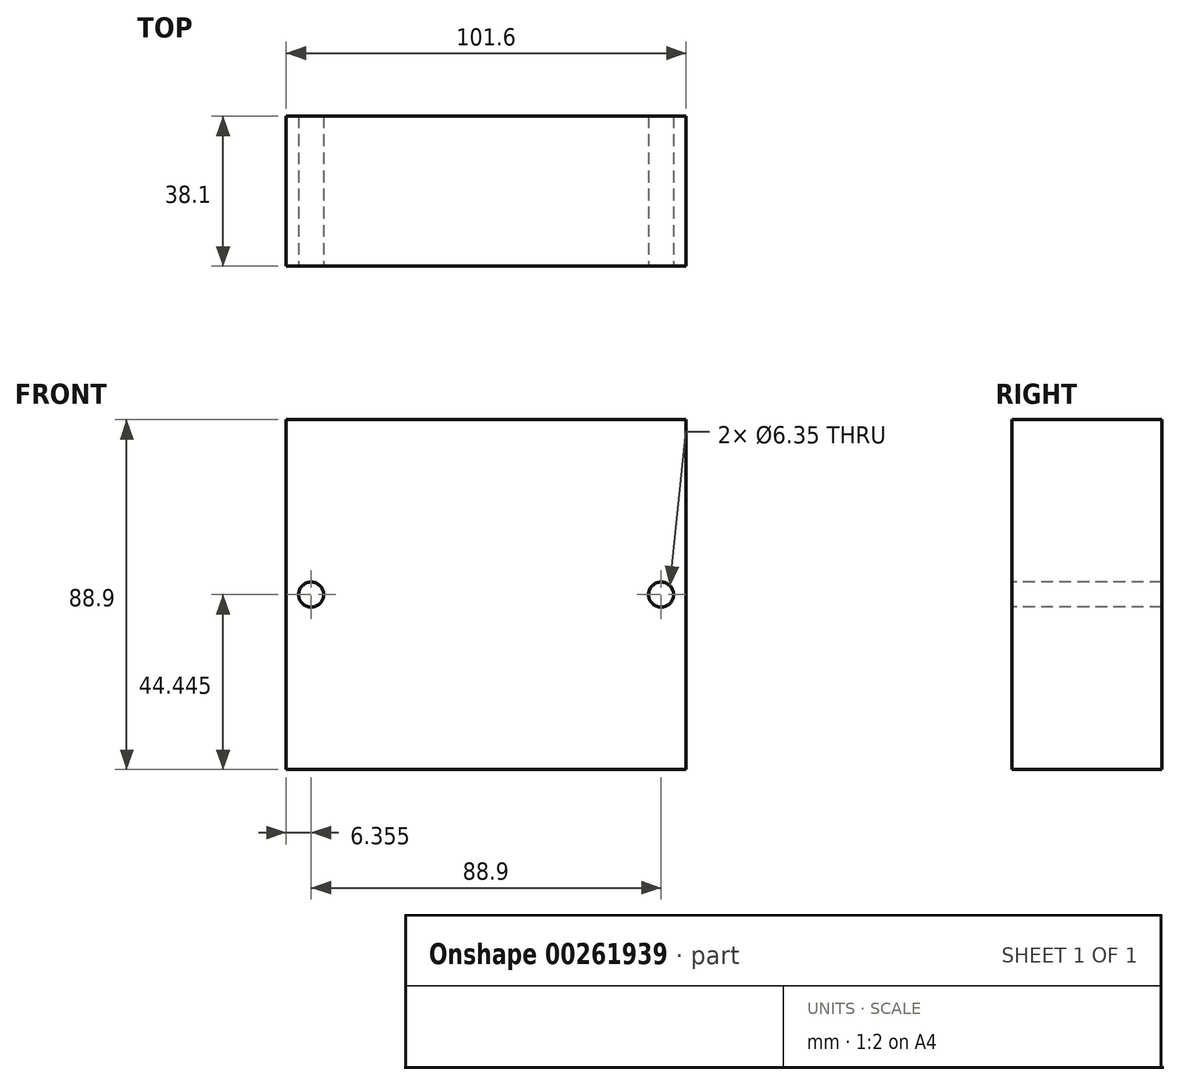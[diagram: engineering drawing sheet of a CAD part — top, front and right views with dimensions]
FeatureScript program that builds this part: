
annotation { "Feature Type Name" : "Feature", "Feature Type Description" : "" }
export const myFeature = defineFeature(function(context is Context, id is Id, definition is map)
    precondition{}
    {
        {
            var Q0;
            Q0=qCreatedBy(makeId("Front.planeOp"),FACE);
            var sketch = newSketch(context, id + "F0", { "sketchPlane" : qUnion([Q0])});
            skLineSegment(sketch, "E0.bottom", {"start": v(-28.5, 53.95) * mm, "end": v(73.1, 53.95) * mm});
            skLineSegment(sketch, "E0.top", {"start": v(-28.5, -34.95) * mm, "end": v(73.1, -34.95) * mm});
            skLineSegment(sketch, "E0.left", {"start": v(-28.5, 53.95) * mm, "end": v(-28.5, -34.95) * mm});
            skLineSegment(sketch, "E0.right", {"start": v(73.1, 53.95) * mm, "end": v(73.1, -34.95) * mm});
            skSolve(sketch);
        }
        {
            var Q0;
            Q0=makeQuery(id+"F0.imprint","IMPRINT",FACE,{"disambiguationData":[TD([[makeQuery(id+"F0.imprint","IMPRINT",EDGE,{"derivedFrom":sQuery(id+"F0.wireOp",EDGE,"E0.bottom")}),-1.0]])]});
            extrude(context, id + "F1", {"entities" : qUnion([Q0]), "depth" : 38.1 * mm});
        }
        {
            var Q0;
            Q0=makeQuery(id+"F1.opExtrude","CAP_FACE",FACE,{"disambiguationData":[OSD([sQuery(id+"F0.wireOp",EDGE,"E0.bottom"),sQuery(id+"F0.wireOp",EDGE,"E0.top"),sQuery(id+"F0.wireOp",EDGE,"E0.left"),sQuery(id+"F0.wireOp",EDGE,"E0.right")])],"isStart":false});
            var sketch = newSketch(context, id + "F2", { "sketchPlane" : qUnion([Q0])});
            skPoint(sketch, "E1", {"position": v(-22.16, 9.5) * mm});
            skPoint(sketch, "E2", {"position": v(66.74, 9.5) * mm});
            skSolve(sketch);
        }
        {
            var Q0;
            Q0=sQuery(id+"F2.wireOp",VERTEX,"E1");
            var Q1;
            Q1=makeQuery(id+"F1.opExtrude","SWEPT_BODY",BODY,{"disambiguationData":[OSD([sQuery(id+"F0.wireOp",EDGE,"E0.bottom"),sQuery(id+"F0.wireOp",EDGE,"E0.top"),sQuery(id+"F0.wireOp",EDGE,"E0.left"),sQuery(id+"F0.wireOp",EDGE,"E0.right")])]});
            hole(context, id + "F3", {"style" : HoleStyle.SIMPLE, "endStyle" : HoleEndStyle.THROUGH, "holeDiameter" : 6.35 * mm, "tappedDepth" : 12.7 * mm, "tapClearance" : 3, "locations" : qUnion([Q0]), "scope" : qUnion([Q1])});
        }
        {
            var Q0;
            Q0=sQuery(id+"F2.wireOp",VERTEX,"E2");
            var Q1;
            Q1=makeQuery(id+"F1.opExtrude","SWEPT_BODY",BODY,{"disambiguationData":[OSD([sQuery(id+"F0.wireOp",EDGE,"E0.bottom"),sQuery(id+"F0.wireOp",EDGE,"E0.top"),sQuery(id+"F0.wireOp",EDGE,"E0.left"),sQuery(id+"F0.wireOp",EDGE,"E0.right")])]});
            hole(context, id + "F4", {"style" : HoleStyle.SIMPLE, "endStyle" : HoleEndStyle.THROUGH, "holeDiameter" : 6.35 * mm, "tappedDepth" : 12.7 * mm, "tapClearance" : 3, "locations" : qUnion([Q0]), "scope" : qUnion([Q1])});
        }
    });
